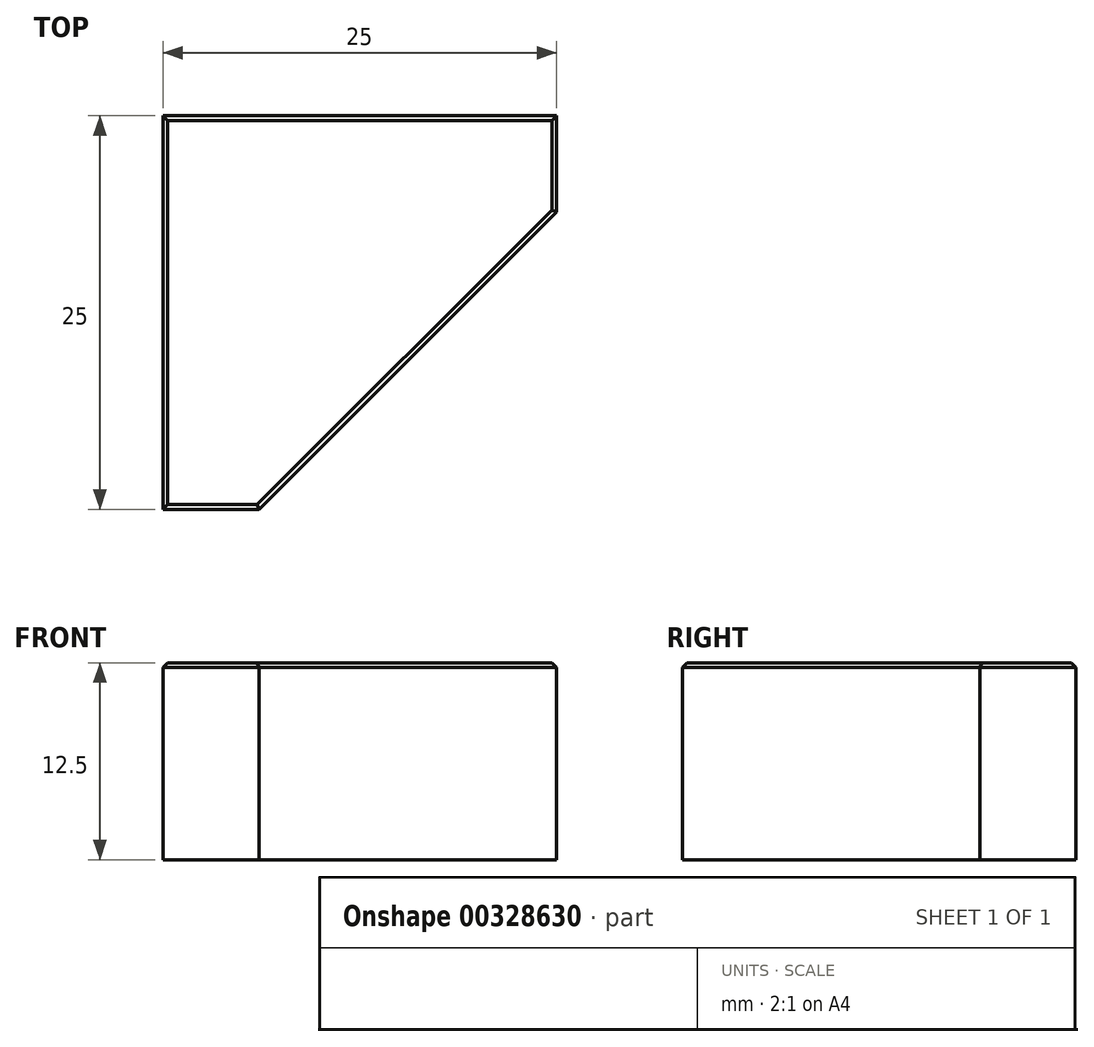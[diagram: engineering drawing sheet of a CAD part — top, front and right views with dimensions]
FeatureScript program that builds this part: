
annotation { "Feature Type Name" : "Feature", "Feature Type Description" : "" }
export const myFeature = defineFeature(function(context is Context, id is Id, definition is map)
    precondition{}
    {
        {
            var Q0;
            Q0=qCreatedBy(makeId("Top.planeOp"),FACE);
            var sketch = newSketch(context, id + "F0", { "sketchPlane" : qUnion([Q0])});
            skLineSegment(sketch, "E0.bottom", {"start": v(25, 0) * mm, "end": v(0, 0) * mm});
            skLineSegment(sketch, "E0.top", {"start": v(6.1, -25) * mm, "end": v(0, -25) * mm});
            skLineSegment(sketch, "E0.right", {"start": v(0, 0) * mm, "end": v(0, -25) * mm});
            skLineSegment(sketch, "E1", {"start": v(6.1, -25) * mm, "end": v(25, -6.1) * mm});
            skLineSegment(sketch, "E2", {"start": v(25, 0) * mm, "end": v(25, -6.1) * mm});
            skSolve(sketch);
        }
        {
            var Q0;
            Q0=qSketchRegion(id+"F0",true);
            extrude(context, id + "F1", {"entities" : qUnion([Q0]), "oppositeDirection" : true, "depth" : 12.5 * mm});
        }
        {
            var Q0;
            Q0=makeQuery(id+"F1.opExtrude","CAP_FACE",FACE,{"disambiguationData":[OSD([sQuery(id+"F0.wireOp",EDGE,"E0.bottom"),sQuery(id+"F0.wireOp",EDGE,"E0.top"),sQuery(id+"F0.wireOp",EDGE,"E0.left"),sQuery(id+"F0.wireOp",EDGE,"E0.right")])],"isStart":true});
            chamfer(context, id + "F2", {"entities" : qUnion([Q0]), "width" : .3 * mm, "tangentPropagation" : true});
        }
    });
